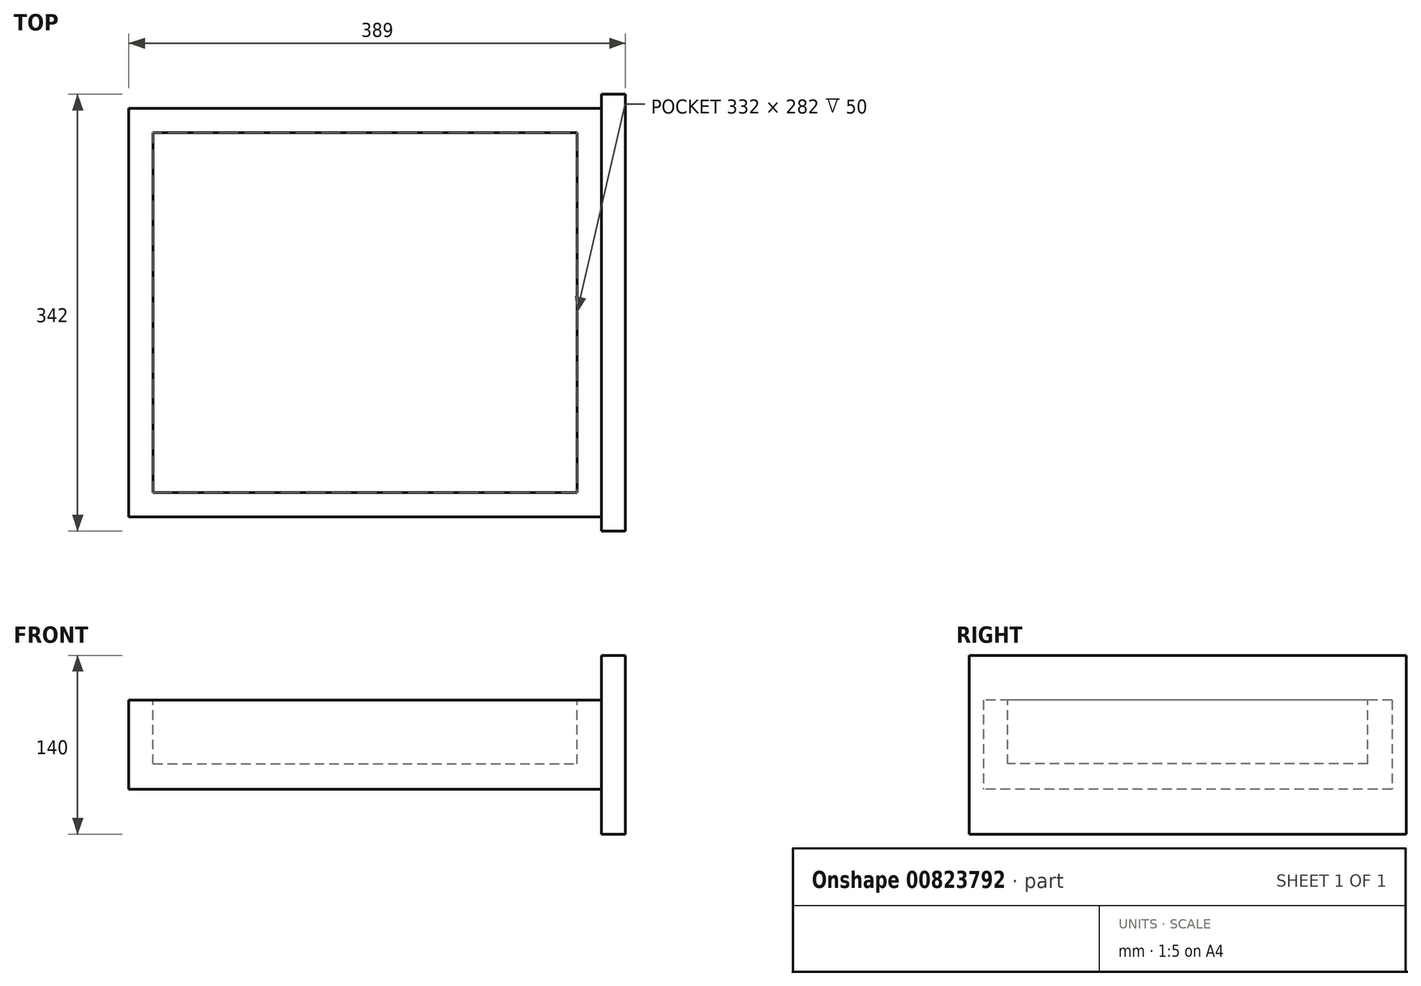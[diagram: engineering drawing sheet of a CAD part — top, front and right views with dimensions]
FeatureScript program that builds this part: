
annotation { "Feature Type Name" : "Feature", "Feature Type Description" : "" }
export const myFeature = defineFeature(function(context is Context, id is Id, definition is map)
    precondition{}
    {
        {
            var Q0;
            Q0=qCreatedBy(makeId("Top.planeOp"),FACE);
            var sketch = newSketch(context, id + "F0", { "sketchPlane" : qUnion([Q0])});
            skLineSegment(sketch, "E0.bottom", {"start": v(-185, 160) * mm, "end": v(185, 160) * mm});
            skLineSegment(sketch, "E0.top", {"start": v(-185, -160) * mm, "end": v(185, -160) * mm});
            skLineSegment(sketch, "E0.left", {"start": v(-185, 160) * mm, "end": v(-185, -160) * mm});
            skLineSegment(sketch, "E0.right", {"start": v(185, 160) * mm, "end": v(185, -160) * mm});
            skPoint(sketch, "E0.middle", {"position": v(0, 0) * mm});
            skSolve(sketch);
        }
        {
            var Q0;
            Q0 = qSketchRegion(id + "F0", true);
            extrude(context, id + "F1", {"entities" : qUnion([Q0]), "depth" : 70 * mm, "offsetDistance" : 25 * mm});
        }
        {
            var Q0;
            Q0=makeQuery(id+"F1.opExtrude","CAP_FACE",FACE,{"disambiguationData":[OSD([sQuery(id+"F0.wireOp",EDGE,"E0.bottom"),sQuery(id+"F0.wireOp",EDGE,"E0.top"),sQuery(id+"F0.wireOp",EDGE,"E0.left"),sQuery(id+"F0.wireOp",EDGE,"E0.right")])],"isStart":false});
            var sketch = newSketch(context, id + "F2", { "sketchPlane" : qUnion([Q0])});
            skLineSegment(sketch, "E1.bottom", {"start": v(-166, 141) * mm, "end": v(166, 141) * mm});
            skLineSegment(sketch, "E1.top", {"start": v(-166, -141) * mm, "end": v(166, -141) * mm});
            skLineSegment(sketch, "E1.left", {"start": v(-166, 141) * mm, "end": v(-166, -141) * mm});
            skLineSegment(sketch, "E1.right", {"start": v(166, 141) * mm, "end": v(166, -141) * mm});
            skPoint(sketch, "E1.middle", {"position": v(0, 0) * mm});
            skSolve(sketch);
        }
        {
            var Q0;
            Q0 = qSketchRegion(id + "F2", true);
            extrude(context, id + "F3", {"entities" : qUnion([Q0]), "operationType" : NewBodyOperationType.REMOVE, "oppositeDirection" : true, "depth" : 50 * mm, "offsetDistance" : 25 * mm});
        }
        {
            var Q0;
            Q0=makeQuery(id+"F1.opExtrude","SWEPT_FACE",FACE,{"disambiguationData":[OSD([sQuery(id+"F0.wireOp",EDGE,"E0.right")])]});
            var sketch = newSketch(context, id + "F4", { "sketchPlane" : qUnion([Q0])});
            skLineSegment(sketch, "E2.bottom", {"start": v(171, -35) * mm, "end": v(-171, -35) * mm});
            skLineSegment(sketch, "E2.top", {"start": v(171, 105) * mm, "end": v(-171, 105) * mm});
            skLineSegment(sketch, "E2.left", {"start": v(171, -35) * mm, "end": v(171, 105) * mm});
            skLineSegment(sketch, "E2.right", {"start": v(-171, -35) * mm, "end": v(-171, 105) * mm});
            skPoint(sketch, "E2.middle", {"position": v(0, 35) * mm});
            skPoint(sketch, "E2.middle.positionSnap0", {"position": v(-160, 35) * mm});
            skPoint(sketch, "E2.middle.positionSnap1", {"position": v(0, 70) * mm});
            skPoint(sketch, "E2.centerSnap0", {"position": v(-160, 35) * mm});
            skPoint(sketch, "E2.centerSnap1", {"position": v(0, 70) * mm});
            skSolve(sketch);
        }
        {
            var Q0;
            Q0 = qSketchRegion(id + "F4", true);
            extrude(context, id + "F5", {"entities" : qUnion([Q0]), "operationType" : NewBodyOperationType.ADD, "depth" : 19 * mm, "offsetDistance" : 25 * mm});
        }
    });
